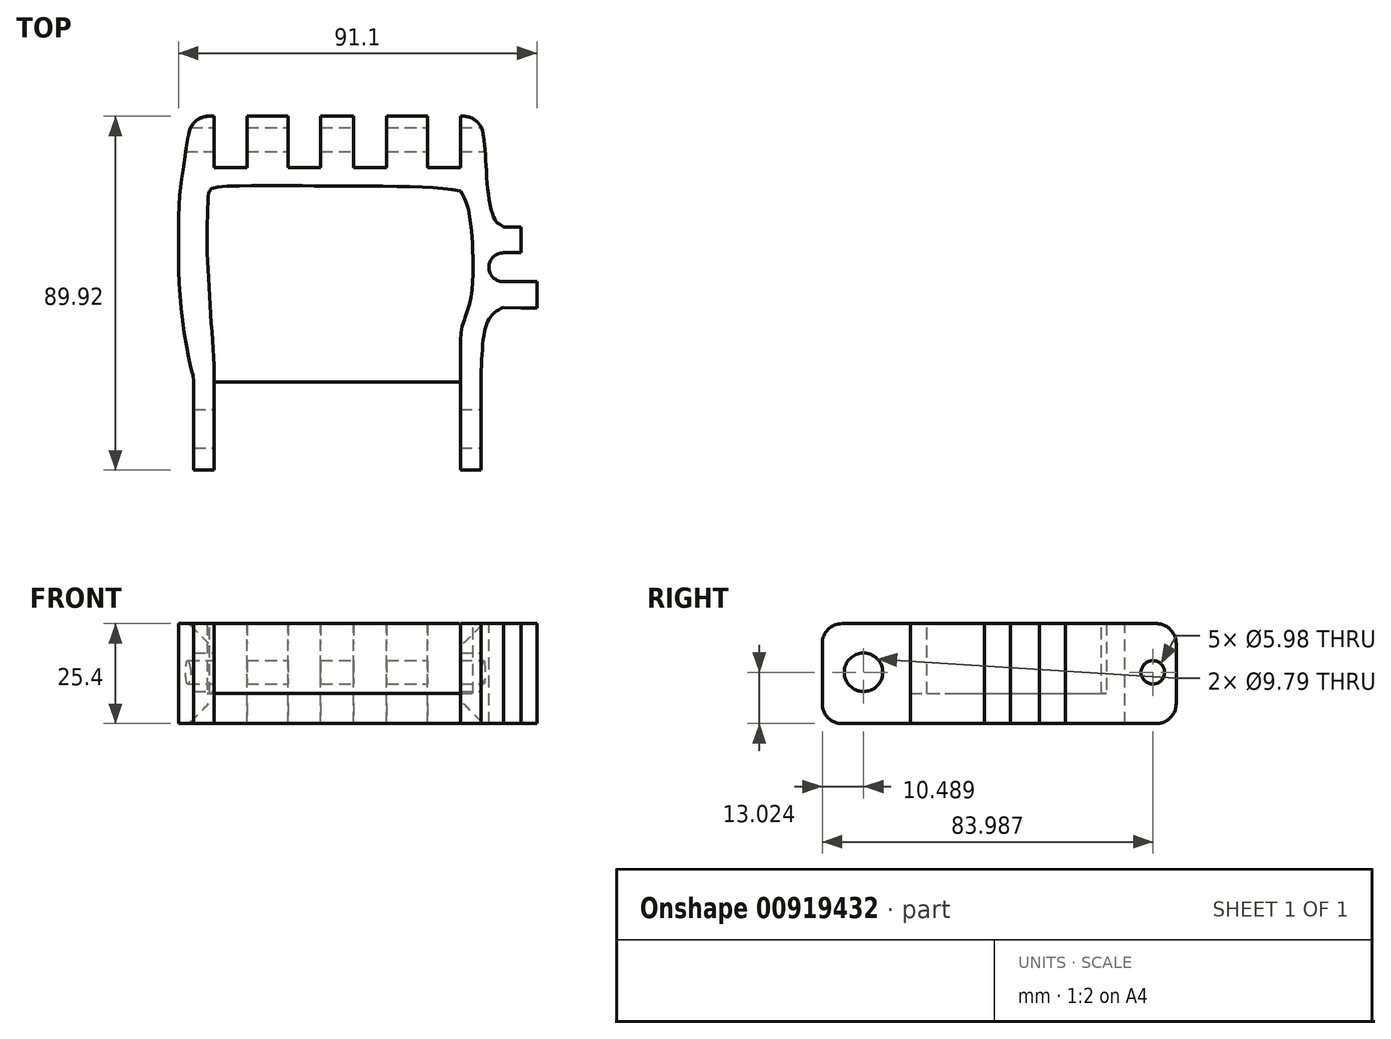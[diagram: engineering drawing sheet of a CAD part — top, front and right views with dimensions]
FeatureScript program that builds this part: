
annotation { "Feature Type Name" : "Feature", "Feature Type Description" : "" }
export const myFeature = defineFeature(function(context is Context, id is Id, definition is map)
    precondition{}
    {
        {
            var Q0;
            Q0=qCreatedBy(makeId("Top.planeOp"),FACE);
            var sketch = newSketch(context, id + "F0", { "sketchPlane" : qUnion([Q0])});
            skLineSegment(sketch, "E0", {"start": v(-36.33, 48.78) * mm, "end": v(-31.12, 48.78) * mm});
            skLineSegment(sketch, "E1", {"start": v(-36.33, 48.78) * mm, "end": v(-36.33, -41.14) * mm});
            skLineSegment(sketch, "E2", {"start": v(-36.33, -41.14) * mm, "end": v(-31.12, -41.14) * mm});
            skLineSegment(sketch, "E3", {"start": v(36.62, -41.14) * mm, "end": v(36.62, 48.78) * mm});
            skLineSegment(sketch, "E4", {"start": v(-36.33, -18.78) * mm, "end": v(36.62, -18.78) * mm});
            skLineSegment(sketch, "E5", {"start": v(-31.12, -18.78) * mm, "end": v(-31.12, -41.14) * mm});
            skLineSegment(sketch, "E6", {"start": v(31.41, -18.78) * mm, "end": v(31.41, -41.14) * mm});
            skLineSegment(sketch, "E7", {"start": v(-36.33, -35.79) * mm, "end": v(-31.12, -35.79) * mm, "construction": true});
            skLineSegment(sketch, "E8", {"start": v(31.41, -29.96) * mm, "end": v(36.62, -29.96) * mm, "construction": true});
            skLineSegment(sketch, "E9.trimOffspring", {"start": v(31.41, -41.14) * mm, "end": v(36.62, -41.14) * mm});
            skPoint(sketch, "E10.endSnap0", {"position": v(0.15, 15) * mm});
            skPoint(sketch, "E11.orphan", {"position": v(0.15, 48.78) * mm});
            skPoint(sketch, "E12.orphan", {"position": v(0.15, -18.78) * mm});
            skPoint(sketch, "E13.start.orphan", {"position": v(0.15, 23.27) * mm});
            skFitSpline(sketch, "E14", {"points": [v(-36.33, 48.78) * mm, v(-38.96, 35.72) * mm, v(-39.92, 27.88) * mm, v(-40.16, 11.1) * mm, v(-38.85, -5.67) * mm, v(-36.69, -16.39) * mm, v(-36.33, -18.78) * mm], "startDerivative": vector(-21.2, -53.04) * mm, "endDerivative": vector(5.57, -77.66) * mm});
            skLineSegment(sketch, "E15", {"start": v(36.62, 35.72) * mm, "end": v(-36.33, 35.72) * mm});
            skLineSegment(sketch, "E16", {"start": v(36.62, 20.62) * mm, "end": v(42.36, 20.62) * mm});
            skLineSegment(sketch, "E17", {"start": v(42.36, 20.62) * mm, "end": v(42.36, 0.19) * mm, "construction": true});
            skLineSegment(sketch, "E18", {"start": v(42.36, 0.19) * mm, "end": v(36.62, 0.19) * mm});
            skLineSegment(sketch, "E19", {"start": v(-31.12, -18.78) * mm, "end": v(-31.12, 35.72) * mm, "construction": true});
            skLineSegment(sketch, "E20", {"start": v(31.41, -18.78) * mm, "end": v(31.41, 35.72) * mm, "construction": true});
            skLineSegment(sketch, "E21", {"start": v(-22.79, 48.78) * mm, "end": v(-22.79, 35.72) * mm});
            skPoint(sketch, "E21.endSnap0", {"position": v(0.15, 35.72) * mm});
            skLineSegment(sketch, "E22", {"start": v(23.08, 48.78) * mm, "end": v(23.08, 35.72) * mm});
            skLineSegment(sketch, "E23", {"start": v(-22.79, 48.78) * mm, "end": v(-12.37, 48.78) * mm, "construction": true});
            skLineSegment(sketch, "E24", {"start": v(23.08, 48.78) * mm, "end": v(12.66, 48.78) * mm, "construction": true});
            skLineSegment(sketch, "E25", {"start": v(-12.37, 48.78) * mm, "end": v(-12.37, 35.72) * mm});
            skLineSegment(sketch, "E26", {"start": v(-4.04, 48.78) * mm, "end": v(-4.04, 35.72) * mm});
            skLineSegment(sketch, "E27", {"start": v(4.33, 48.78) * mm, "end": v(4.33, 35.72) * mm});
            skLineSegment(sketch, "E28", {"start": v(12.66, 48.78) * mm, "end": v(12.66, 35.72) * mm});
            skLineSegment(sketch, "E29.trimOffspring", {"start": v(-22.79, 48.78) * mm, "end": v(-12.37, 48.78) * mm});
            skLineSegment(sketch, "E30.trimOffspring", {"start": v(-4.04, 48.78) * mm, "end": v(4.33, 48.78) * mm});
            skLineSegment(sketch, "E31.trimOffspring", {"start": v(12.66, 48.78) * mm, "end": v(23.08, 48.78) * mm});
            skLineSegment(sketch, "E32.trimOffspring", {"start": v(31.41, 48.78) * mm, "end": v(36.62, 48.78) * mm});
            skLineSegment(sketch, "E33", {"start": v(-31.12, 48.78) * mm, "end": v(-31.12, 35.72) * mm});
            skLineSegment(sketch, "E34", {"start": v(31.41, 48.78) * mm, "end": v(31.41, 35.72) * mm});
            skLineSegment(sketch, "E35", {"start": v(42.36, 20.62) * mm, "end": v(42.36, 14.08) * mm});
            skLineSegment(sketch, "E36", {"start": v(42.36, 0.19) * mm, "end": v(42.36, 6.71) * mm});
            skLineSegment(sketch, "E37", {"start": v(42.36, 14.08) * mm, "end": v(36.62, 14.08) * mm});
            skLineSegment(sketch, "E38", {"start": v(42.36, 6.71) * mm, "end": v(36.62, 6.71) * mm});
            skLineSegment(sketch, "E39", {"start": v(42.36, 20.62) * mm, "end": v(46.82, 20.62) * mm});
            skLineSegment(sketch, "E40", {"start": v(42.36, 14.08) * mm, "end": v(46.82, 14.08) * mm});
            skLineSegment(sketch, "E41", {"start": v(46.82, 14.08) * mm, "end": v(46.82, 20.62) * mm});
            skLineSegment(sketch, "E42", {"start": v(42.36, 6.71) * mm, "end": v(46.82, 6.71) * mm});
            skLineSegment(sketch, "E43", {"start": v(46.82, 6.71) * mm, "end": v(46.82, 0) * mm});
            skLineSegment(sketch, "E44", {"start": v(46.82, 0) * mm, "end": v(42.36, 0.19) * mm});
            skLineSegment(sketch, "E45", {"start": v(46.82, 6.71) * mm, "end": v(50.88, 6.71) * mm});
            skLineSegment(sketch, "E46", {"start": v(50.88, 6.71) * mm, "end": v(50.88, 0) * mm});
            skLineSegment(sketch, "E47", {"start": v(50.88, 0) * mm, "end": v(46.82, 0) * mm});
            skArc(sketch, "E48", {"start": v(42.36, 14.08) * mm, "mid": v(38.67, 10.4) * mm, "end": v(42.36, 6.71) * mm});
            skFitSpline(sketch, "E49", {"points": [v(42.36, 20.62) * mm, v(41.84, 21.05) * mm, v(40.86, 21.65) * mm, v(39.94, 23) * mm, v(38.53, 28.98) * mm, v(37.82, 38.47) * mm, v(37.17, 44.6) * mm, v(36.62, 48.78) * mm], "startDerivative": vector(-7.4, 7.12) * mm, "endDerivative": vector(-6.12, 25.7) * mm});
            skFitSpline(sketch, "E50", {"points": [v(42.36, 0.19) * mm, v(40.31, -0.95) * mm, v(38.09, -4.02) * mm, v(36.62, -18.78) * mm], "startDerivative": vector(-9.93, -4.66) * mm, "endDerivative": vector(-0.98, -33.26) * mm});
            skSolve(sketch);
        }
        {
            var Q0;
            {var subQ1=sQuery(id+"F0.wireOp",EDGE,"E3");var subQ14=makeQuery(id+"F0.imprint","INTERSECT",VERTEX,{"derivedFrom":[subQ1,sQuery(id+"F0.wireOp",EDGE,"E18")]});Q0=makeQuery(id+"F0.imprint","IMPRINT",FACE,{"disambiguationData":[TD([[makeQuery(id+"F0.imprint","IMPRINT",EDGE,{"disambiguationData":[TD([[subQ14,-1.0]])],"derivedFrom":subQ1}),1.0]])]});}
            var Q1;
            {var subQ0=sQuery(id+"F0.wireOp",EDGE,"E0");Q1=makeQuery(id+"F0.imprint","IMPRINT",FACE,{"disambiguationData":[TD([[makeQuery(id+"F0.imprint","IMPRINT",EDGE,{"derivedFrom":subQ0}),-1.0]])]});}
            var Q2;
            {var subQ0=sQuery(id+"F0.wireOp",EDGE,"E14");Q2=makeQuery(id+"F0.imprint","IMPRINT",FACE,{"disambiguationData":[TD([[makeQuery(id+"F0.imprint","IMPRINT",EDGE,{"derivedFrom":subQ0}),1.0]])]});}
            var Q3;
            {var subQ0=sQuery(id+"F0.wireOp",EDGE,"E21");Q3=makeQuery(id+"F0.imprint","IMPRINT",FACE,{"disambiguationData":[TD([[makeQuery(id+"F0.imprint","IMPRINT",EDGE,{"derivedFrom":subQ0}),1.0]])]});}
            var Q4;
            {var subQ0=sQuery(id+"F0.wireOp",EDGE,"E26");Q4=makeQuery(id+"F0.imprint","IMPRINT",FACE,{"disambiguationData":[TD([[makeQuery(id+"F0.imprint","IMPRINT",EDGE,{"derivedFrom":subQ0}),1.0]])]});}
            var Q5;
            {var subQ0=sQuery(id+"F0.wireOp",EDGE,"E22");Q5=makeQuery(id+"F0.imprint","IMPRINT",FACE,{"disambiguationData":[TD([[makeQuery(id+"F0.imprint","IMPRINT",EDGE,{"derivedFrom":subQ0}),-1.0]])]});}
            var Q6;
            {var subQ0=sQuery(id+"F0.wireOp",EDGE,"E32.trimOffspring");Q6=makeQuery(id+"F0.imprint","IMPRINT",FACE,{"disambiguationData":[TD([[makeQuery(id+"F0.imprint","IMPRINT",EDGE,{"derivedFrom":subQ0}),-1.0]])]});}
            var Q7;
            {var subQ2=sQuery(id+"F0.wireOp",EDGE,"E16");Q7=makeQuery(id+"F0.imprint","IMPRINT",FACE,{"disambiguationData":[TD([[makeQuery(id+"F0.imprint","IMPRINT",EDGE,{"derivedFrom":subQ2}),1.0]])]});}
            var Q8;
            {var subQ0=sQuery(id+"F0.wireOp",EDGE,"E16");Q8=makeQuery(id+"F0.imprint","IMPRINT",FACE,{"disambiguationData":[TD([[makeQuery(id+"F0.imprint","IMPRINT",EDGE,{"derivedFrom":subQ0}),-1.0]])]});}
            var Q9;
            Q9=makeQuery(id+"F0.imprint","IMPRINT",FACE,{"disambiguationData":[TD([[makeQuery(id+"F0.imprint","IMPRINT",EDGE,{"derivedFrom":sQuery(id+"F0.wireOp",EDGE,"E35")}),1.0]])]});
            var Q10;
            {var subQ0=sQuery(id+"F0.wireOp",EDGE,"E37");Q10=makeQuery(id+"F0.imprint","IMPRINT",FACE,{"disambiguationData":[TD([[makeQuery(id+"F0.imprint","IMPRINT",EDGE,{"derivedFrom":subQ0}),1.0]])]});}
            var Q11;
            {var subQ0=sQuery(id+"F0.wireOp",EDGE,"E18");Q11=makeQuery(id+"F0.imprint","IMPRINT",FACE,{"disambiguationData":[TD([[makeQuery(id+"F0.imprint","IMPRINT",EDGE,{"derivedFrom":subQ0}),-1.0]])]});}
            var Q12;
            Q12=makeQuery(id+"F0.imprint","IMPRINT",FACE,{"disambiguationData":[TD([[makeQuery(id+"F0.imprint","IMPRINT",EDGE,{"derivedFrom":sQuery(id+"F0.wireOp",EDGE,"E36")}),-1.0]])]});
            var Q13;
            Q13=makeQuery(id+"F0.imprint","IMPRINT",FACE,{"disambiguationData":[TD([[makeQuery(id+"F0.imprint","IMPRINT",EDGE,{"derivedFrom":sQuery(id+"F0.wireOp",EDGE,"E43")}),1.0]])]});
            var Q14;
            {var subQ2=sQuery(id+"F0.wireOp",EDGE,"E18");Q14=makeQuery(id+"F0.imprint","IMPRINT",FACE,{"disambiguationData":[TD([[makeQuery(id+"F0.imprint","IMPRINT",EDGE,{"derivedFrom":subQ2}),1.0]])]});}
            var Q15;
            {var subQ4=sQuery(id+"F0.wireOp",EDGE,"E6");Q15=makeQuery(id+"F0.imprint","IMPRINT",FACE,{"disambiguationData":[TD([[makeQuery(id+"F0.imprint","IMPRINT",EDGE,{"derivedFrom":subQ4}),1.0]])]});}
            var Q16;
            {var subQ0=sQuery(id+"F0.wireOp",EDGE,"E2");Q16=makeQuery(id+"F0.imprint","IMPRINT",FACE,{"disambiguationData":[TD([[makeQuery(id+"F0.imprint","IMPRINT",EDGE,{"derivedFrom":subQ0}),1.0]])]});}
            extrude(context, id + "F1", {"entities" : qUnion([Q0, Q1, Q2, Q3, Q4, Q5, Q6, Q7, Q8, Q9, Q10, Q11, Q12, Q13, Q14, Q15, Q16]), "oppositeDirection" : true, "depth" : 25.4 * mm, "offsetDistance" : 25.4 * mm});
        }
        {
            var Q0;
            Q0=makeQuery(id+"F1.opExtrude","CAP_EDGE",EDGE,{"disambiguationData":[OSD([sQuery(id+"F0.wireOp",EDGE,"E29.trimOffspring")])],"isStart":false});
            var Q1;
            Q1=makeQuery(id+"F1.opExtrude","CAP_EDGE",EDGE,{"disambiguationData":[OSD([sQuery(id+"F0.wireOp",EDGE,"E29.trimOffspring")])],"isStart":true});
            var Q2;
            Q2=makeQuery(id+"F1.opExtrude","CAP_EDGE",EDGE,{"disambiguationData":[OSD([sQuery(id+"F0.wireOp",EDGE,"E0")])],"isStart":true});
            var Q3;
            Q3=makeQuery(id+"F1.opExtrude","CAP_EDGE",EDGE,{"disambiguationData":[OSD([sQuery(id+"F0.wireOp",EDGE,"E0")])],"isStart":false});
            var Q4;
            Q4=makeQuery(id+"F1.opExtrude","SWEPT_EDGE",EDGE,{"disambiguationData":[OSD([sQuery(id+"F0.wireOp",EDGE,"E0"),sQuery(id+"F0.wireOp",EDGE,"E1"),sQuery(id+"F0.wireOp",EDGE,"E14")])]});
            var Q5;
            Q5=makeQuery(id+"F1.opExtrude","CAP_EDGE",EDGE,{"disambiguationData":[OSD([sQuery(id+"F0.wireOp",EDGE,"E30.trimOffspring")])],"isStart":true});
            var Q6;
            Q6=makeQuery(id+"F1.opExtrude","CAP_EDGE",EDGE,{"disambiguationData":[OSD([sQuery(id+"F0.wireOp",EDGE,"E30.trimOffspring")])],"isStart":false});
            var Q7;
            Q7=makeQuery(id+"F1.opExtrude","CAP_EDGE",EDGE,{"disambiguationData":[OSD([sQuery(id+"F0.wireOp",EDGE,"E31.trimOffspring")])],"isStart":false});
            var Q8;
            Q8=makeQuery(id+"F1.opExtrude","CAP_EDGE",EDGE,{"disambiguationData":[OSD([sQuery(id+"F0.wireOp",EDGE,"E31.trimOffspring")])],"isStart":true});
            var Q9;
            Q9=makeQuery(id+"F1.opExtrude","CAP_EDGE",EDGE,{"disambiguationData":[OSD([sQuery(id+"F0.wireOp",EDGE,"E32.trimOffspring")])],"isStart":false});
            var Q10;
            Q10=makeQuery(id+"F1.opExtrude","CAP_EDGE",EDGE,{"disambiguationData":[OSD([sQuery(id+"F0.wireOp",EDGE,"E32.trimOffspring")])],"isStart":true});
            var Q11;
            Q11=makeQuery(id+"F1.opExtrude","SWEPT_EDGE",EDGE,{"disambiguationData":[OSD([sQuery(id+"F0.wireOp",EDGE,"E3"),sQuery(id+"F0.wireOp",EDGE,"E32.trimOffspring"),sQuery(id+"F0.wireOp",EDGE,"E49")])]});
            var Q12;
            Q12=makeQuery(id+"F1.opExtrude","CAP_EDGE",EDGE,{"disambiguationData":[OSD([sQuery(id+"F0.wireOp",EDGE,"E2")])],"isStart":false});
            var Q13;
            Q13=makeQuery(id+"F1.opExtrude","CAP_EDGE",EDGE,{"disambiguationData":[OSD([sQuery(id+"F0.wireOp",EDGE,"E2")])],"isStart":true});
            var Q14;
            Q14=makeQuery(id+"F1.opExtrude","CAP_EDGE",EDGE,{"disambiguationData":[OSD([sQuery(id+"F0.wireOp",EDGE,"E9.trimOffspring")])],"isStart":false});
            var Q15;
            Q15=makeQuery(id+"F1.opExtrude","CAP_EDGE",EDGE,{"disambiguationData":[OSD([sQuery(id+"F0.wireOp",EDGE,"E9.trimOffspring")])],"isStart":true});
            fillet(context, id + "F2", {"entities" : qUnion([Q0, Q1, Q2, Q3, Q4, Q5, Q6, Q7, Q8, Q9, Q10, Q11, Q12, Q13, Q14, Q15]), "radius" : 5.08 * mm, "tangentPropagation" : true, "allowEdgeOverflow" : false});
        }
        {
            var Q0;
            Q0=qCreatedBy(makeId("Top.planeOp"),FACE);
            var sketch = newSketch(context, id + "F3", { "sketchPlane" : qUnion([Q0])});
            skLineSegment(sketch, "E51", {"start": v(-31.12, -18.78) * mm, "end": v(31.42, -18.78) * mm});
            skLineSegment(sketch, "E52", {"start": v(31.42, -18.78) * mm, "end": v(31.42, 29.75) * mm});
            skLineSegment(sketch, "E53", {"start": v(-31.12, -18.78) * mm, "end": v(-31.12, 29.75) * mm});
            skLineSegment(sketch, "E54", {"start": v(-31.12, 29.75) * mm, "end": v(31.42, 29.75) * mm});
            skFitSpline(sketch, "E55", {"points": [v(-31.12, -14.54) * mm, v(-31.96, -2.32) * mm, v(-32.77, 11.19) * mm, v(-32.9, 20.89) * mm, v(-32.64, 28.42) * mm, v(-32.23, 29.75) * mm, v(-31.12, 29.75) * mm], "startDerivative": vector(-3.57, 51.9) * mm, "endDerivative": vector(18.62, -3.27) * mm});
            skFitSpline(sketch, "E56", {"points": [v(-32.23, 29.75) * mm, v(-31.55, 30.46) * mm, v(-20.68, 31.1) * mm, v(-10.99, 31.1) * mm, v(4.81, 31.02) * mm, v(22.75, 30.72) * mm, v(31.42, 29.75) * mm], "startDerivative": vector(6.26, 14.5) * mm, "endDerivative": vector(49.22, -10.82) * mm});
            skFitSpline(sketch, "E57", {"points": [v(31.42, -8.23) * mm, v(32.67, -2.26) * mm, v(34.3, 3.95) * mm, v(34.6, 13.3) * mm, v(34.17, 20.4) * mm, v(32.9, 26.91) * mm, v(31.42, 29.75) * mm], "startDerivative": vector(0, 53.13) * mm, "endDerivative": vector(-10.75, 19.92) * mm});
            skSolve(sketch);
        }
        {
            var Q0;
            Q0 = qSketchRegion(id + "F3", true);
            extrude(context, id + "F4", {"entities" : qUnion([Q0]), "operationType" : NewBodyOperationType.REMOVE, "oppositeDirection" : true, "depth" : 17.78 * mm, "offsetDistance" : 25.4 * mm});
        }
        {
            var Q0;
            Q0=qCreatedBy(makeId("Right.planeOp"),FACE);
            var sketch = newSketch(context, id + "F5", { "sketchPlane" : qUnion([Q0])});
            skCircle(sketch, "E58", {"center": v(-30.65, -12.38) * mm, "radius": 4.9 * mm});
            skCircle(sketch, "E59", {"center": v(42.85, -12.38) * mm, "radius": 3 * mm});
            skPoint(sketch, "E60.center.orphan", {"position": v(39.86, -12.38) * mm});
            skSolve(sketch);
        }
        {
            var Q0;
            Q0 = qSketchRegion(id + "F5", true);
            extrude(context, id + "F6", {"entities" : qUnion([Q0]), "operationType" : NewBodyOperationType.REMOVE, "oppositeDirection" : true, "depth" : 52.07 * mm, "offsetDistance" : 25.4 * mm, "hasSecondDirection" : true, "secondDirectionOppositeDirection" : false, "secondDirectionDepth" : 40.9 * mm});
        }
    });
